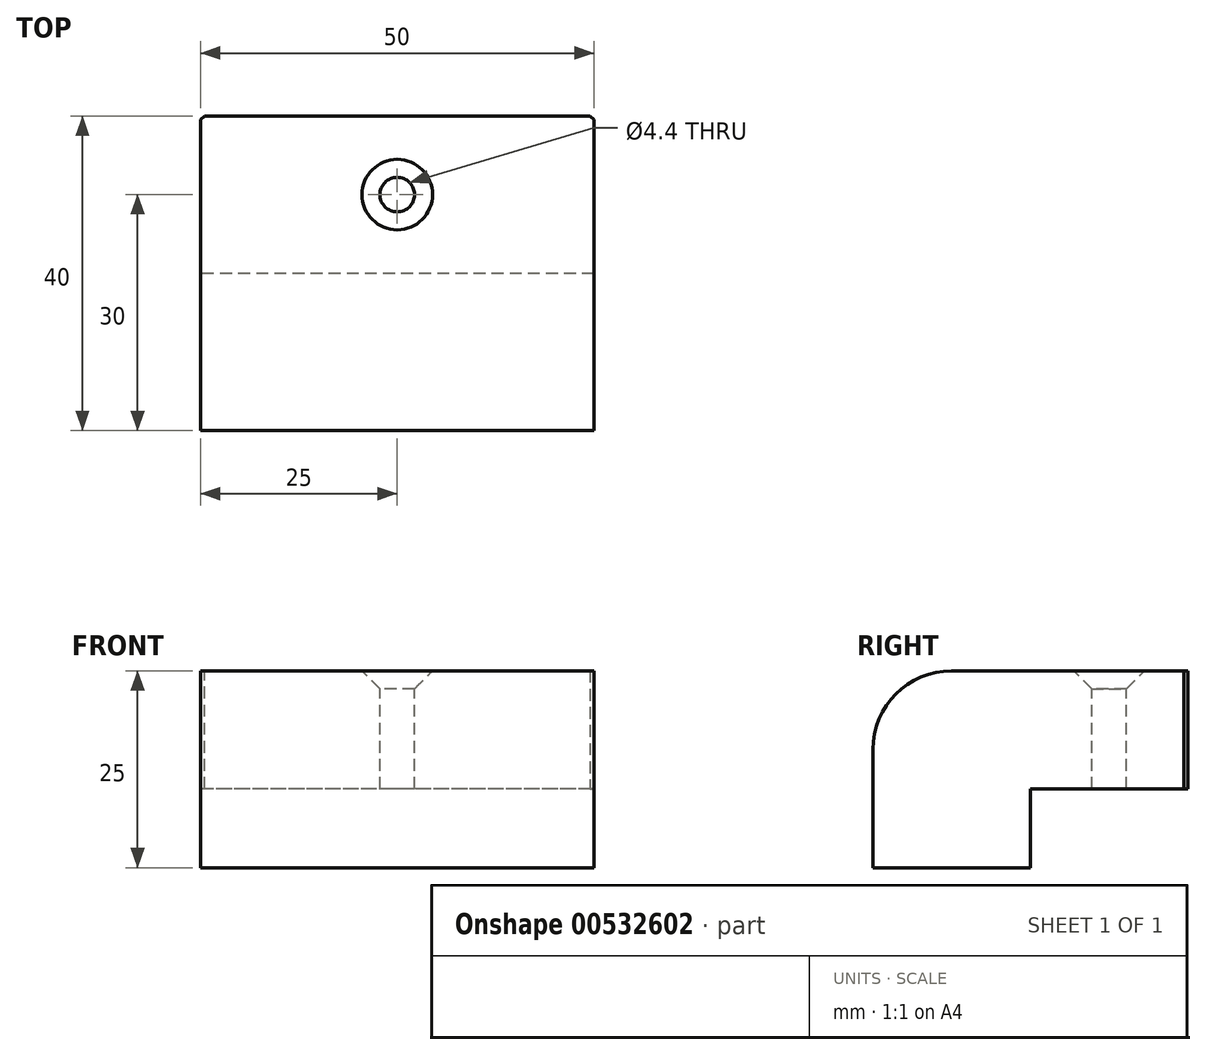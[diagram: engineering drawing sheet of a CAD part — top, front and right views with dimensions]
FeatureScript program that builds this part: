
annotation { "Feature Type Name" : "Feature", "Feature Type Description" : "" }
export const myFeature = defineFeature(function(context is Context, id is Id, definition is map)
    precondition{}
    {
        {
            var Q0;
            Q0=qCreatedBy(makeId("Top.planeOp"),FACE);
            var sketch = newSketch(context, id + "F0", { "sketchPlane" : qUnion([Q0])});
            skLineSegment(sketch, "E0.bottom", {"start": v(25, 20) * mm, "end": v(-25, 20) * mm});
            skLineSegment(sketch, "E0.top", {"start": v(25, -20) * mm, "end": v(-25, -20) * mm});
            skLineSegment(sketch, "E0.left", {"start": v(25, 20) * mm, "end": v(25, -20) * mm});
            skLineSegment(sketch, "E0.right", {"start": v(-25, 20) * mm, "end": v(-25, -20) * mm});
            skPoint(sketch, "E0.middle", {"position": v(0, 0) * mm});
            skPoint(sketch, "E1", {"position": v(0, 10) * mm});
            skLineSegment(sketch, "E2", {"start": v(25, 0) * mm, "end": v(-25, 0) * mm});
            skSolve(sketch);
        }
        {
            var Q0;
            Q0=makeQuery(id+"F0.imprint","IMPRINT",FACE,{"disambiguationData":[TD([[makeQuery(id+"F0.imprint","IMPRINT",EDGE,{"derivedFrom":sQuery(id+"F0.wireOp",EDGE,"E0.bottom")}),1.0]])]});
            var Q1;
            {var subQ0=sQuery(id+"F0.wireOp",EDGE,"E0.top");Q1=makeQuery(id+"F0.imprint","IMPRINT",FACE,{"disambiguationData":[TD([[makeQuery(id+"F0.imprint","IMPRINT",EDGE,{"derivedFrom":subQ0}),-1.0]])]});}
            extrude(context, id + "F1", {"entities" : qUnion([Q0, Q1]), "depth" : 25 * mm, "offsetDistance" : 25 * mm});
        }
        {
            var Q0;
            {var subQ0=sQuery(id+"F0.wireOp",EDGE,"E0.bottom");Q0=makeQuery(id+"F0.imprint","IMPRINT",FACE,{"disambiguationData":[TD([[makeQuery(id+"F0.imprint","IMPRINT",EDGE,{"derivedFrom":subQ0}),1.0]])]});}
            extrude(context, id + "F2", {"entities" : qUnion([Q0]), "operationType" : NewBodyOperationType.REMOVE, "depth" : 10 * mm, "offsetDistance" : 25 * mm});
        }
        {
            var Q0;
            Q0=makeQuery(id+"F1.opExtrude","SWEPT_FACE",FACE,{"disambiguationData":[OSD([sQuery(id+"F0.wireOp",EDGE,"E0.right")])]});
            var sketch = newSketch(context, id + "F3", { "sketchPlane" : qUnion([Q0])});
            skLineSegment(sketch, "E3", {"start": v(0, 10) * mm, "end": v(0, 0) * mm});
            skLineSegment(sketch, "E4", {"start": v(0, 0) * mm, "end": v(20, 0) * mm});
            skLineSegment(sketch, "E5", {"start": v(20, 15) * mm, "end": v(20, 0) * mm});
            skLineSegment(sketch, "E6", {"start": v(-20, 25) * mm, "end": v(10, 25) * mm});
            skLineSegment(sketch, "E7", {"start": v(-20, 25) * mm, "end": v(-20, 10) * mm});
            skLineSegment(sketch, "E8", {"start": v(-20, 10) * mm, "end": v(0, 10) * mm});
            skPoint(sketch, "E9.visualSharp", {"position": v(20, 25) * mm});
            skArc(sketch, "E9.filletArc", {"start": v(20, 15) * mm, "mid": v(17.07, 22.07) * mm, "end": v(10, 25) * mm});
            skSolve(sketch);
        }
        {
            var Q0;
            {var subQ0=sQuery(id+"F3.wireOp",EDGE,"E9.filletArc");Q0=makeQuery(id+"F3.imprint","IMPRINT",FACE,{"disambiguationData":[TD([[makeQuery(id+"F3.imprint","IMPRINT",EDGE,{"derivedFrom":subQ0}),-1.0]])]});}
            extrude(context, id + "F4", {"entities" : qUnion([Q0]), "operationType" : NewBodyOperationType.REMOVE, "endBound" : BoundingType.THROUGH_ALL, "oppositeDirection" : true, "depth" : 25 * mm, "offsetDistance" : 25 * mm});
        }
        {
            var Q0;
            Q0=makeQuery(id+"F1.opExtrude","CAP_FACE",FACE,{"disambiguationData":[OSD([sQuery(id+"F0.wireOp",EDGE,"E0.bottom"),sQuery(id+"F0.wireOp",EDGE,"E0.top"),sQuery(id+"F0.wireOp",EDGE,"E0.left"),sQuery(id+"F0.wireOp",EDGE,"E0.right")])],"isStart":false});
            var sketch = newSketch(context, id + "F5", { "sketchPlane" : qUnion([Q0])});
            skPoint(sketch, "E10.0", {"position": v(0, 10) * mm});
            skSolve(sketch);
        }
        {
            var Q0;
            Q0=sQuery(id+"F5.wireOp",VERTEX,"E10.0");
            var Q1;
            Q1=makeQuery(id+"F1.opExtrude","SWEPT_BODY",BODY,{"disambiguationData":[OSD([sQuery(id+"F0.wireOp",EDGE,"E0.bottom"),sQuery(id+"F0.wireOp",EDGE,"E0.top"),sQuery(id+"F0.wireOp",EDGE,"E0.left"),sQuery(id+"F0.wireOp",EDGE,"E0.right")])]});
            hole(context, id + "F6", {"style" : HoleStyle.C_SINK, "endStyle" : HoleEndStyle.THROUGH, "standardTappedOrClearance" : lookupTablePath({ "standard" : "ISO", "fit" : "Normal", "size" : "M4", "type" : "Clearance" }), "standardBlindInLast" : lookupTablePath({ "fit" : "Standard", "standard" : "ISO", "size" : "M4", "type" : "Clearance" }), "holeDiameter" : 4.4 * mm, "cSinkDiameter" : 8.96 * mm, "cSinkAngle" : 90 * degree, "isTappedThrough" : true, "tappedDepth" : 12 * mm, "tapClearance" : 3, "locations" : qUnion([Q0]), "scope" : qUnion([Q1])});
        }
        {
            var Q0;
            Q0=makeQuery(id+"F1.opExtrude","SWEPT_EDGE",EDGE,{"disambiguationData":[OSD([sQuery(id+"F0.wireOp",EDGE,"E0.bottom"),sQuery(id+"F0.wireOp",EDGE,"E0.left")])]});
            var Q1;
            Q1=makeQuery(id+"F1.opExtrude","SWEPT_EDGE",EDGE,{"disambiguationData":[OSD([sQuery(id+"F0.wireOp",EDGE,"E0.bottom"),sQuery(id+"F0.wireOp",EDGE,"E0.right")])]});
            chamfer(context, id + "F7", {"entities" : qUnion([Q0, Q1]), "width" : 0.5 * mm, "tangentPropagation" : true});
        }
    });
